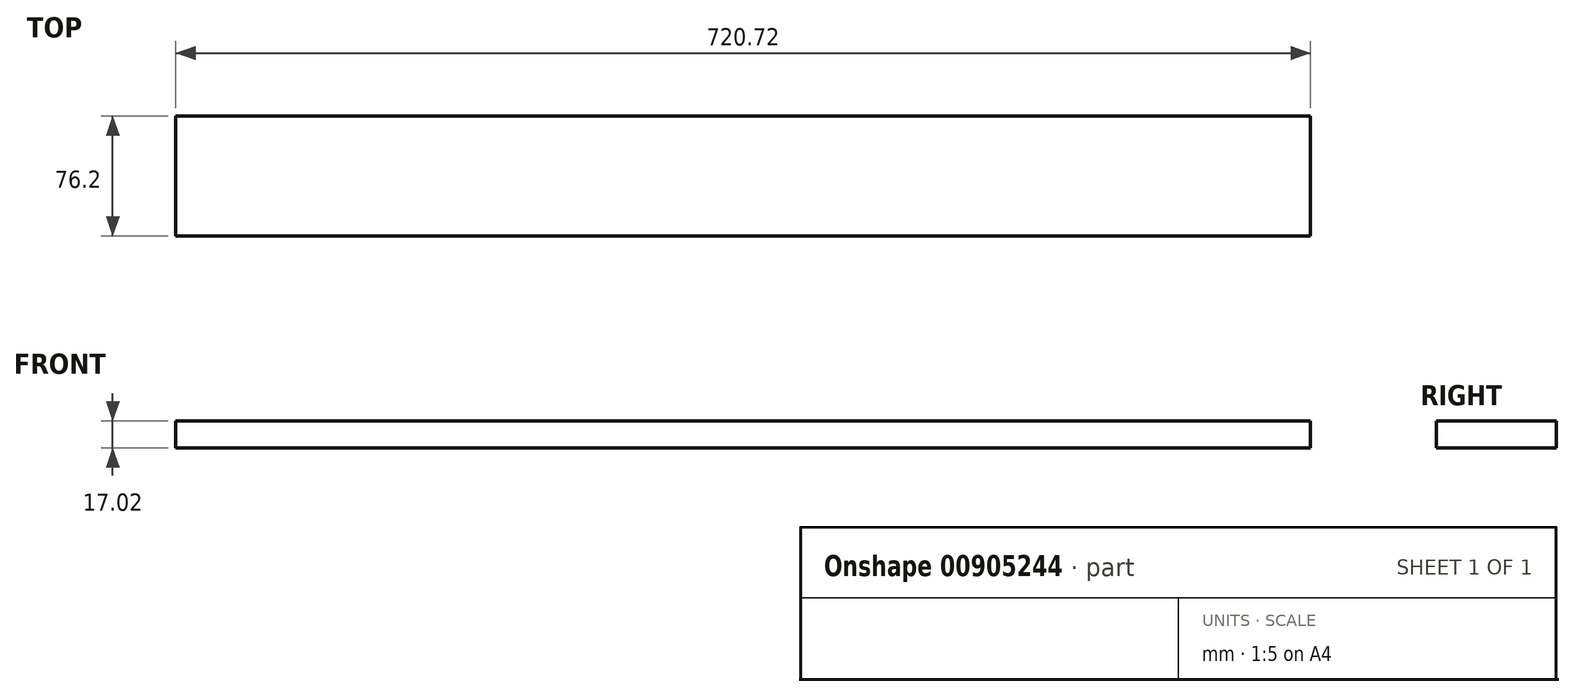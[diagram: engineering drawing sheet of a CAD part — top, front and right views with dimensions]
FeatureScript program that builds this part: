
annotation { "Feature Type Name" : "Feature", "Feature Type Description" : "" }
export const myFeature = defineFeature(function(context is Context, id is Id, definition is map)
    precondition{}
    {
        {
            var Q0;
            Q0=qCreatedBy(makeId("Top.planeOp"),FACE);
            var sketch = newSketch(context, id + "F0", { "sketchPlane" : qUnion([Q0])});
            skLineSegment(sketch, "E0.bottom", {"start": v(360.36, -38.1) * mm, "end": v(-360.36, -38.1) * mm});
            skLineSegment(sketch, "E0.top", {"start": v(360.36, 38.1) * mm, "end": v(-360.36, 38.1) * mm});
            skLineSegment(sketch, "E0.left", {"start": v(360.36, -38.1) * mm, "end": v(360.36, 38.1) * mm});
            skLineSegment(sketch, "E0.right", {"start": v(-360.36, -38.1) * mm, "end": v(-360.36, 38.1) * mm});
            skPoint(sketch, "E0.middle", {"position": v(0, 0) * mm});
            skSolve(sketch);
        }
        {
            var Q0;
            Q0=qSketchRegion(id+"F0",true);
            extrude(context, id + "F1", {"entities" : qUnion([Q0]), "oppositeDirection" : true, "offsetDistance" : 25.4 * mm, "depth" : 17.02 * mm});
        }
    });
